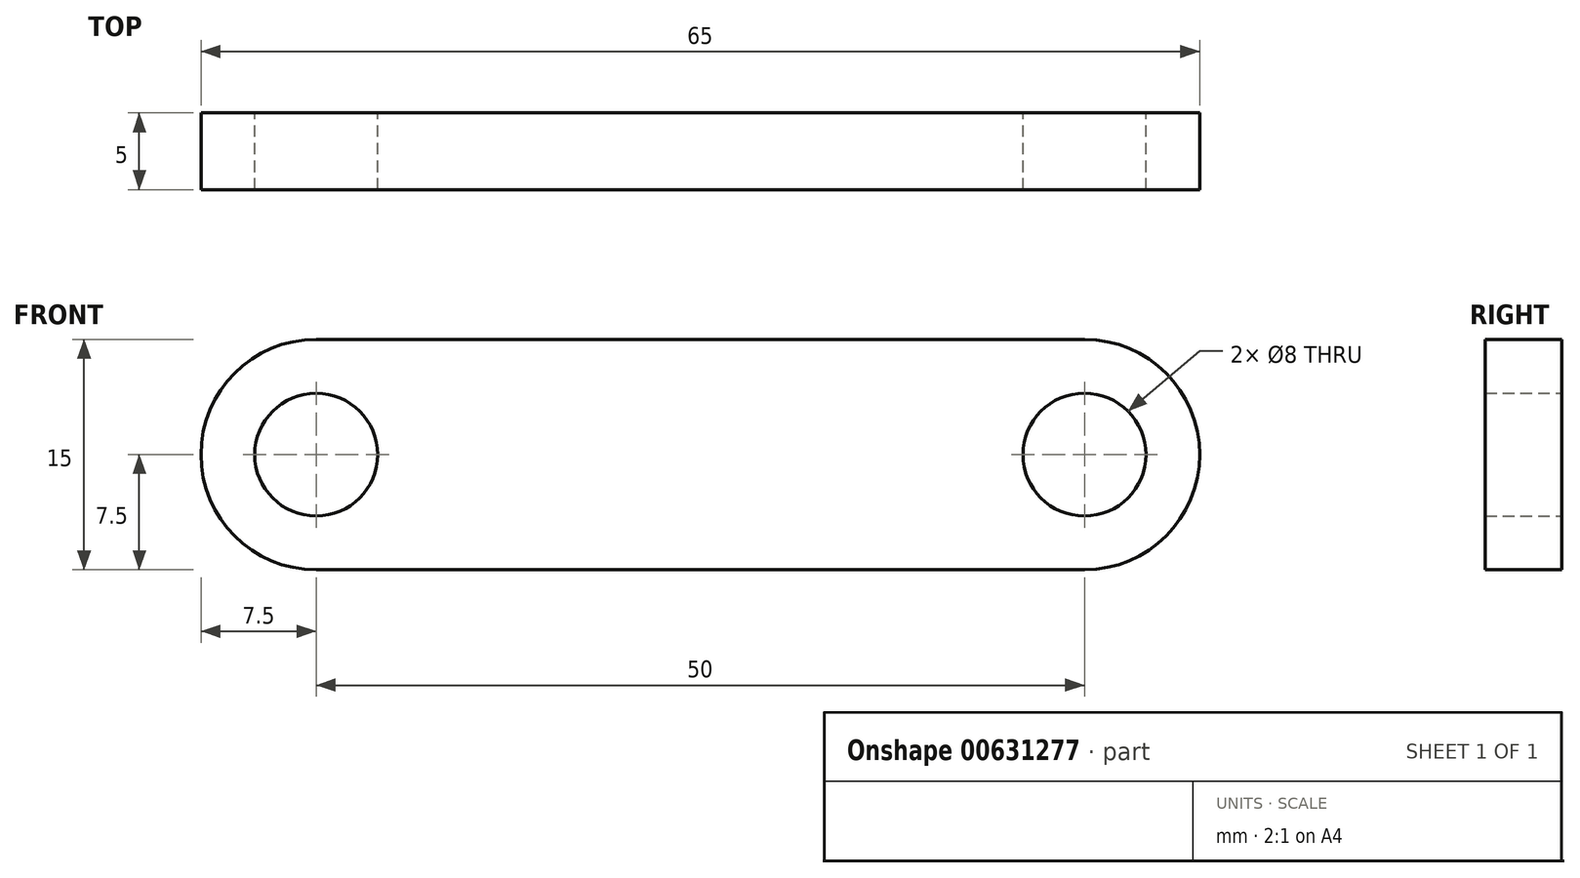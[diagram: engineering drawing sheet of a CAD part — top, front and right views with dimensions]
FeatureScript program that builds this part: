
annotation { "Feature Type Name" : "Feature", "Feature Type Description" : "" }
export const myFeature = defineFeature(function(context is Context, id is Id, definition is map)
    precondition{}
    {
        {
            var Q0;
            Q0=qCreatedBy(makeId("Front.planeOp"),FACE);
            var sketch = newSketch(context, id + "F0", { "sketchPlane" : qUnion([Q0])});
            skLineSegment(sketch, "E0", {"start": v(-44.01, 0) * mm, "end": v(36.83, 0) * mm, "construction": true});
            skArc(sketch, "E1", {"start": v(-25, 7.5) * mm, "mid": v(-32.5, 0) * mm, "end": v(-25, -7.5) * mm});
            skArc(sketch, "E2", {"start": v(25, -7.5) * mm, "mid": v(32.5, 0) * mm, "end": v(25, 7.5) * mm});
            skLineSegment(sketch, "E3", {"start": v(-25, -7.5) * mm, "end": v(25, -7.5) * mm});
            skLineSegment(sketch, "E4", {"start": v(-25, 7.5) * mm, "end": v(25, 7.5) * mm});
            skCircle(sketch, "E5", {"center": v(-25, 0) * mm, "radius": 4 * mm});
            skCircle(sketch, "E6", {"center": v(25, 0) * mm, "radius": 4 * mm});
            skSolve(sketch);
        }
        {
            var Q0;
            Q0 = qSketchRegion(id + "F0", true);
            extrude(context, id + "F1", {"entities" : qUnion([Q0]), "depth" : 5 * mm, "offsetDistance" : 25 * mm});
        }
    });
